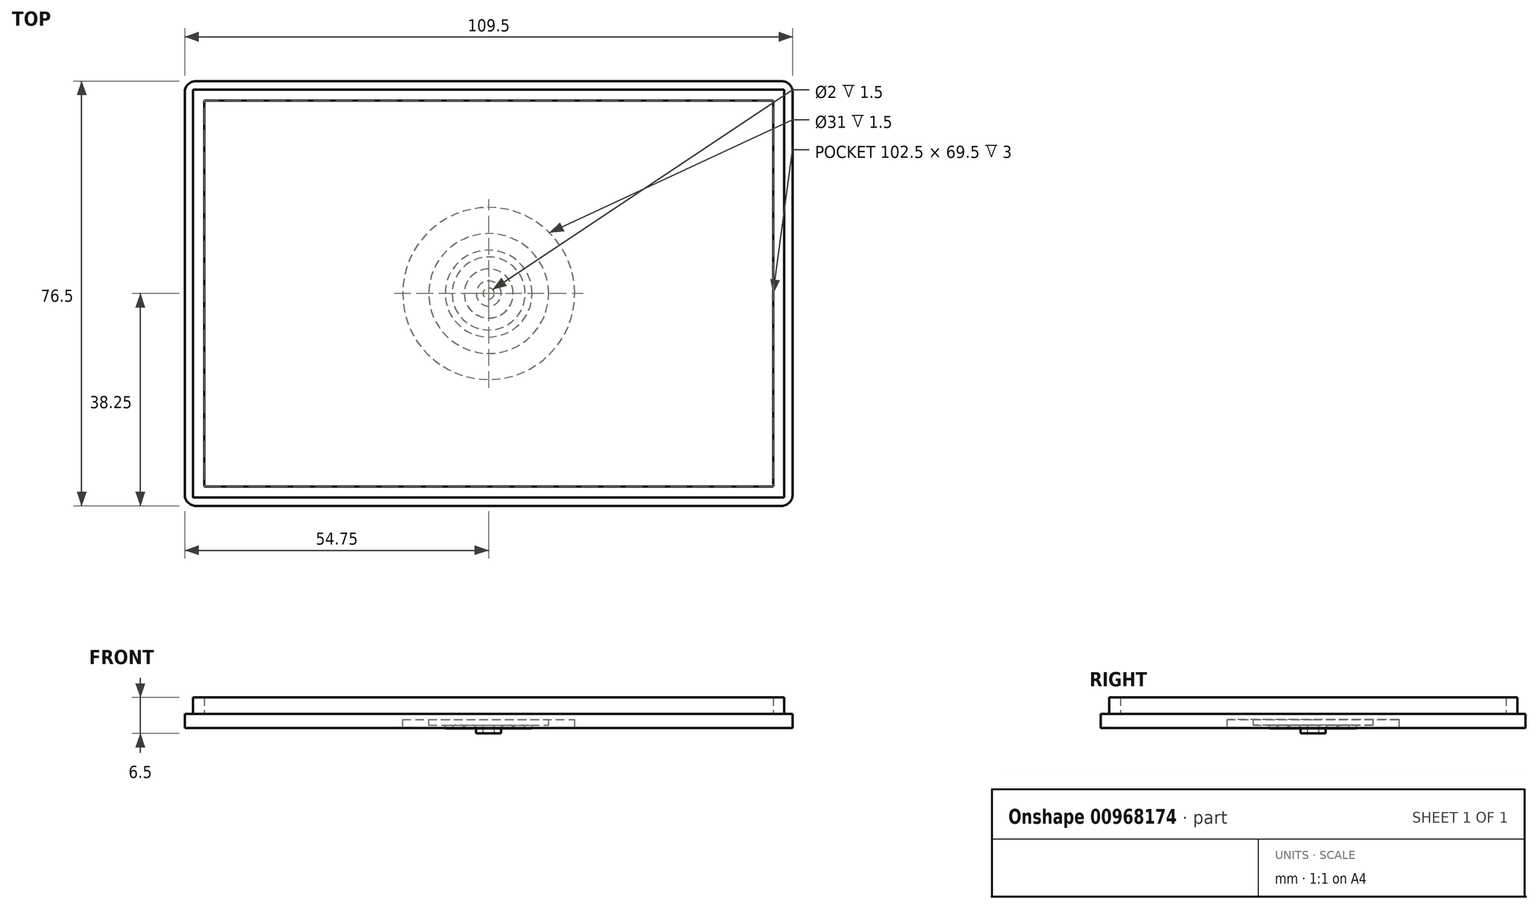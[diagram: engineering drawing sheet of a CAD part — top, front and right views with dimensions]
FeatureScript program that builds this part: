
annotation { "Feature Type Name" : "Feature", "Feature Type Description" : "" }
export const myFeature = defineFeature(function(context is Context, id is Id, definition is map)
    precondition{}
    {
        {
            var Q0;
            Q0=qCreatedBy(makeId("Top.planeOp"),FACE);
            var sketch = newSketch(context, id + "F0", { "sketchPlane" : qUnion([Q0])});
            skLineSegment(sketch, "E0.bottom", {"start": v(51.25, 34.75) * mm, "end": v(-51.25, 34.75) * mm});
            skLineSegment(sketch, "E0.top", {"start": v(51.25, -34.75) * mm, "end": v(-51.25, -34.75) * mm});
            skLineSegment(sketch, "E0.left", {"start": v(51.25, 34.75) * mm, "end": v(51.25, -34.75) * mm});
            skLineSegment(sketch, "E0.right", {"start": v(-51.25, 34.75) * mm, "end": v(-51.25, -34.75) * mm});
            skPoint(sketch, "E0.middle", {"position": v(0, 0) * mm});
            skSolve(sketch);
        }
        {
            var Q0;
            Q0=qCreatedBy(makeId("Top.planeOp"),FACE);
            var sketch = newSketch(context, id + "F1", { "sketchPlane" : qUnion([Q0])});
            skLineSegment(sketch, "E1.0", {"start": v(53.25, 36.75) * mm, "end": v(-53.25, 36.75) * mm});
            skLineSegment(sketch, "E1.1", {"start": v(53.25, 36.75) * mm, "end": v(53.25, -36.75) * mm});
            skLineSegment(sketch, "E1.2", {"start": v(53.25, -36.75) * mm, "end": v(-53.25, -36.75) * mm});
            skLineSegment(sketch, "E1.3", {"start": v(-53.25, 36.75) * mm, "end": v(-53.25, -36.75) * mm});
            skSolve(sketch);
        }
        {
            var Q0;
            Q0=qCreatedBy(makeId("Top.planeOp"),FACE);
            var sketch = newSketch(context, id + "F2", { "sketchPlane" : qUnion([Q0])});
            skLineSegment(sketch, "E2.0", {"start": v(54.75, 38.25) * mm, "end": v(-54.75, 38.25) * mm});
            skLineSegment(sketch, "E2.1", {"start": v(54.75, 38.25) * mm, "end": v(54.75, -38.25) * mm});
            skLineSegment(sketch, "E2.2", {"start": v(54.75, -38.25) * mm, "end": v(-54.75, -38.25) * mm});
            skLineSegment(sketch, "E2.3", {"start": v(-54.75, 38.25) * mm, "end": v(-54.75, -38.25) * mm});
            skSolve(sketch);
        }
        {
            var Q0;
            Q0 = qSketchRegion(id + "F2", true);
            extrude(context, id + "F3", {"entities" : qUnion([Q0]), "oppositeDirection" : true, "depth" : 1 * mm, "offsetDistance" : 25 * mm});
        }
        {
            var Q0;
            Q0 = qSketchRegion(id + "F1", true);
            extrude(context, id + "F4", {"entities" : qUnion([Q0]), "operationType" : NewBodyOperationType.ADD, "depth" : 3 * mm, "offsetDistance" : 25 * mm});
        }
        {
            var Q0;
            Q0 = qSketchRegion(id + "F0", true);
            extrude(context, id + "F5", {"entities" : qUnion([Q0]), "operationType" : NewBodyOperationType.REMOVE, "endBound" : BoundingType.UP_TO_NEXT, "depth" : 25 * mm, "offsetDistance" : 25 * mm});
        }
        {
            var Q0;
            Q0=makeQuery(id+"F3.opExtrude","CAP_FACE",FACE,{"disambiguationData":[OSD([sQuery(id+"F2.wireOp",EDGE,"E2.0"),sQuery(id+"F2.wireOp",EDGE,"E2.1"),sQuery(id+"F2.wireOp",EDGE,"E2.2"),sQuery(id+"F2.wireOp",EDGE,"E2.3")])],"isStart":false});
            var sketch = newSketch(context, id + "F6", { "sketchPlane" : qUnion([Q0])});
            skCircle(sketch, "E3", {"center": v(0, 0) * mm, "radius": 10.8 * mm});
            skSolve(sketch);
        }
        {
            var Q0;
            Q0 = qSketchRegion(id + "F6", true);
            extrude(context, id + "F7", {"entities" : qUnion([Q0]), "operationType" : NewBodyOperationType.ADD, "depth" : 1 * mm, "offsetDistance" : 25 * mm});
        }
        {
            var Q0;
            Q0=makeQuery(id+"F3.opExtrude","CAP_FACE",FACE,{"disambiguationData":[OSD([sQuery(id+"F2.wireOp",EDGE,"E2.0"),sQuery(id+"F2.wireOp",EDGE,"E2.1"),sQuery(id+"F2.wireOp",EDGE,"E2.2"),sQuery(id+"F2.wireOp",EDGE,"E2.3")])],"isStart":false});
            var sketch = newSketch(context, id + "F8", { "sketchPlane" : qUnion([Q0])});
            skCircle(sketch, "E4", {"center": v(0, 0) * mm, "radius": 2.25 * mm});
            skCircle(sketch, "E5", {"center": v(0, 0) * mm, "radius": 1 * mm});
            skSolve(sketch);
        }
        {
            var Q0;
            Q0 = qSketchRegion(id + "F8", true);
            extrude(context, id + "F9", {"entities" : qUnion([Q0]), "operationType" : NewBodyOperationType.ADD, "depth" : 2.5 * mm, "offsetDistance" : 25 * mm});
        }
        {
            var Q0;
            {var subQ0=sQuery(id+"F6.wireOp",EDGE,"E3");Q0=makeQuery(id+"F9.boolean.opBoolean","SPLIT",FACE,{"disambiguationData":[TD([makeQuery(id+"F7.opExtrude","SWEPT_FACE",FACE,{"disambiguationData":[OSD([subQ0])]})])],"derivedFrom":makeQuery(id+"F7.opExtrude","CAP_FACE",FACE,{"disambiguationData":[OSD([subQ0])],"isStart":false})});}
            var sketch = newSketch(context, id + "F10", { "sketchPlane" : qUnion([Q0])});
            skCircle(sketch, "E6", {"center": v(0, 0) * mm, "radius": 7.83 * mm});
            skCircle(sketch, "E7", {"center": v(0, 0) * mm, "radius": 6.58 * mm});
            skSolve(sketch);
        }
        {
            var Q0;
            Q0 = qSketchRegion(id + "F10", true);
            extrude(context, id + "F11", {"entities" : qUnion([Q0]), "operationType" : NewBodyOperationType.ADD, "depth" : .6 * mm, "offsetDistance" : 25 * mm});
        }
        {
            var Q0;
            {var subQ0=makeQuery(id+"F9.opExtrude","SWEPT_FACE",FACE,{"disambiguationData":[OSD([sQuery(id+"F8.wireOp",EDGE,"E4")])]});var subQ1=sQuery(id+"F6.wireOp",EDGE,"E3");Q0=makeQuery(id+"F11.boolean.opBoolean","SPLIT",FACE,{"disambiguationData":[TD([subQ0])],"derivedFrom":makeQuery(id+"F9.boolean.opBoolean","SPLIT",FACE,{"disambiguationData":[TD([makeQuery(id+"F7.opExtrude","SWEPT_FACE",FACE,{"disambiguationData":[OSD([subQ1])]})])],"derivedFrom":makeQuery(id+"F7.opExtrude","CAP_FACE",FACE,{"disambiguationData":[OSD([subQ1])],"isStart":false})})});}
            var sketch = newSketch(context, id + "F12", { "sketchPlane" : qUnion([Q0])});
            skCircle(sketch, "E8.0", {"center": v(0, 0) * mm, "radius": 6.58 * mm, "construction": true});
            skCircle(sketch, "E9.0", {"center": v(0, 0) * mm, "radius": 2.25 * mm, "construction": true});
            skCircle(sketch, "E10.0.0", {"center": v(0, 0) * mm, "radius": 7.83 * mm, "construction": true});
            skCircle(sketch, "E11", {"center": v(0, 0) * mm, "radius": 4.41 * mm});
            skLineSegment(sketch, "E12", {"start": v(2.25, 0) * mm, "end": v(6.58, 0) * mm, "construction": true});
            skPoint(sketch, "E13", {"position": v(4.41, 0) * mm});
            skCircle(sketch, "E14", {"center": v(0, 0) * mm, "radius": 4.42 * mm});
            skSolve(sketch);
        }
        {
            var Q0;
            Q0 = qSketchRegion(id + "F12", true);
            extrude(context, id + "F13", {"entities" : qUnion([Q0]), "operationType" : NewBodyOperationType.ADD, "depth" : .6 * mm, "offsetDistance" : 25 * mm});
        }
        {
            var Q0;
            Q0=makeQuery(id+"F13.opExtrude","CAP_EDGE",EDGE,{"disambiguationData":[OSD([sQuery(id+"F12.wireOp",EDGE,"E14")])],"isStart":true});
            var Q1;
            {var subQ0=makeQuery(id+"F11.opExtrude","SWEPT_FACE",FACE,{"disambiguationData":[OSD([sQuery(id+"F10.wireOp",EDGE,"E7")])]});var subQ1=makeQuery(id+"F9.opExtrude","SWEPT_FACE",FACE,{"disambiguationData":[OSD([sQuery(id+"F8.wireOp",EDGE,"E4")])]});var subQ2=sQuery(id+"F6.wireOp",EDGE,"E3");Q1=makeQuery(id+"F13.boolean.opBoolean","SPLIT",FACE,{"disambiguationData":[TD([subQ0])],"derivedFrom":makeQuery(id+"F11.boolean.opBoolean","SPLIT",FACE,{"disambiguationData":[TD([subQ1])],"derivedFrom":makeQuery(id+"F9.boolean.opBoolean","SPLIT",FACE,{"disambiguationData":[TD([makeQuery(id+"F7.opExtrude","SWEPT_FACE",FACE,{"disambiguationData":[OSD([subQ2])]})])],"derivedFrom":makeQuery(id+"F7.opExtrude","CAP_FACE",FACE,{"disambiguationData":[OSD([subQ2])],"isStart":false})})})});}
            var Q2;
            Q2=makeQuery(id+"F9.boolean.opBoolean","INTERSECT",EDGE,{"derivedFrom":[makeQuery(id+"F7.opExtrude","CAP_FACE",FACE,{"disambiguationData":[OSD([sQuery(id+"F6.wireOp",EDGE,"E3")])],"isStart":false}),makeQuery(id+"F9.opExtrude","SWEPT_FACE",FACE,{"disambiguationData":[OSD([sQuery(id+"F8.wireOp",EDGE,"E4")])]})]});
            var Q3;
            Q3=makeQuery(id+"F13.opExtrude","CAP_EDGE",EDGE,{"disambiguationData":[OSD([sQuery(id+"F12.wireOp",EDGE,"E11")])],"isStart":true});
            fillet(context, id + "F14", {"entities" : qUnion([Q0, Q1, Q2, Q3]), "radius" : .6 * mm, "tangentPropagation" : true, "allowEdgeOverflow" : false});
        }
        {
            var Q0;
            Q0=makeQuery(id+"F3.opExtrude","SWEPT_EDGE",EDGE,{"disambiguationData":[OSD([sQuery(id+"F2.wireOp",EDGE,"E2.2"),sQuery(id+"F2.wireOp",EDGE,"E2.3")])]});
            var Q1;
            Q1=makeQuery(id+"F3.opExtrude","SWEPT_EDGE",EDGE,{"disambiguationData":[OSD([sQuery(id+"F2.wireOp",EDGE,"E2.1"),sQuery(id+"F2.wireOp",EDGE,"E2.2")])]});
            var Q2;
            Q2=makeQuery(id+"F3.opExtrude","SWEPT_EDGE",EDGE,{"disambiguationData":[OSD([sQuery(id+"F2.wireOp",EDGE,"E2.0"),sQuery(id+"F2.wireOp",EDGE,"E2.1")])]});
            var Q3;
            Q3=makeQuery(id+"F3.opExtrude","SWEPT_EDGE",EDGE,{"disambiguationData":[OSD([sQuery(id+"F2.wireOp",EDGE,"E2.0"),sQuery(id+"F2.wireOp",EDGE,"E2.3")])]});
            fillet(context, id + "F15", {"entities" : qUnion([Q0, Q1, Q2, Q3]), "radius" : 2 * mm, "tangentPropagation" : true, "allowEdgeOverflow" : false});
        }
        {
            var Q0;
            Q0=makeQuery(id+"F3.opExtrude","CAP_FACE",FACE,{"disambiguationData":[OSD([sQuery(id+"F2.wireOp",EDGE,"E2.0"),sQuery(id+"F2.wireOp",EDGE,"E2.1"),sQuery(id+"F2.wireOp",EDGE,"E2.2"),sQuery(id+"F2.wireOp",EDGE,"E2.3")])],"isStart":false});
            var sketch = newSketch(context, id + "F16", { "sketchPlane" : qUnion([Q0])});
            skLineSegment(sketch, "E15.0.0", {"start": v(-54.75, 36.25) * mm, "end": v(-54.75, -36.25) * mm});
            skArc(sketch, "E15.0.1", {"start": v(-54.75, -36.25) * mm, "mid": v(-54.16, -37.66) * mm, "end": v(-52.75, -38.25) * mm});
            skLineSegment(sketch, "E15.0.2", {"start": v(-52.75, -38.25) * mm, "end": v(52.75, -38.25) * mm});
            skArc(sketch, "E15.0.3", {"start": v(52.75, -38.25) * mm, "mid": v(54.16, -37.66) * mm, "end": v(54.75, -36.25) * mm});
            skLineSegment(sketch, "E15.0.4", {"start": v(54.75, -36.25) * mm, "end": v(54.75, 36.25) * mm});
            skArc(sketch, "E15.0.5", {"start": v(54.75, 36.25) * mm, "mid": v(54.16, 37.66) * mm, "end": v(52.75, 38.25) * mm});
            skLineSegment(sketch, "E15.0.6", {"start": v(52.75, 38.25) * mm, "end": v(-52.75, 38.25) * mm});
            skArc(sketch, "E15.0.7", {"start": v(-52.75, 38.25) * mm, "mid": v(-54.16, 37.66) * mm, "end": v(-54.75, 36.25) * mm});
            skCircle(sketch, "E16", {"center": v(0, 0) * mm, "radius": 15.5 * mm});
            skSolve(sketch);
        }
        {
            var Q0;
            Q0 = qSketchRegion(id + "F16", true);
            extrude(context, id + "F17", {"entities" : qUnion([Q0]), "operationType" : NewBodyOperationType.ADD, "depth" : 1.5 * mm, "offsetDistance" : 25 * mm});
        }
    });
